# Revit family: Legrand XL³-S 160 saillie
name_source: partatom
category: Equipement électrique
units: mm (PartAtom-declared; Revit-internal decimal feet)

## family parameters
Basée sur le plan de construction = Non
Configuration du panneau = Deux colonnes, circuits au sein
Cote de connecteur circulaire = Utiliser le diamètre
Couper avec des vides une fois chargée = Non
Numéro OmniClass = 23.80.30.11.17
Partagée = Non
Point de calcul de pièce = Non
Titre OmniClass = Distribution Boards and Control Panels
Toujours verticalement = Oui
Type d'élément = Tableau de raccordement

## types (12) — shared parameters
Conditions Générale d'Utilisation = https://export.legrand.com
ETIM Class 6.0 = EC000261
Fabricant = Legrand
IK = 07
IP = 40
Image du type = XL3S160_saillie_337204_p_230125.jpg
Matière = Acier
RAL = 9003
URL = www.legrand.fr
distance coté zone d'installation = 135 mm  [stored 0.442913 ft]
porte = Oui
profondeur = 135 mm  [stored 0.442913 ft]
zero-valued in all types: Elévation par défaut

## per-type parameters (varying)
- Enveloppe de distribution - XL³ S 160 - Coffret saillie - Métal - 24 modules - 2 rangées: Coffret 337202=Oui; Coffret 337203=Non; Coffret 337204=Non; Coffret 337205=Non; Coffret 337206=Non; Coffret 337207=Non; Coffret 337208=Non; Coffret 337214=Non; Coffret 337215=Non; Coffret 337216=Non; Coffret 337217=Non; Coffret 337218=Non; Description=337202  Enveloppe de distribution - XL³ S 160 - Coffret saillie - Métal - 24 modules - 2 rangées; Hauteur=440 mm  [stored 1.44357 ft]; Largeur=595 mm  [stored 1.9521 ft]; Largeur zone d'installation=865 mm  [stored 2.83793 ft]; distance avant zone d'installation=595 mm  [stored 1.9521 ft]; porte 337252=Oui; porte 337253=Non; porte 337254=Non; porte 337255=Non; porte 337256=Non; porte 337257=Non; porte 337258=Non; porte 337264=Non; porte 337265=Non; porte 337266=Non; porte 337267=Non; porte 337268=Non; profondeur zone d'installation=730 mm  [stored 2.39501 ft]
- Enveloppe de distribution - XL³ S 160 - Coffret saillie - Métal - 24 modules - 3 rangées: Coffret 337202=Non; Coffret 337203=Oui; Coffret 337204=Non; Coffret 337205=Non; Coffret 337206=Non; Coffret 337207=Non; Coffret 337208=Non; Coffret 337214=Non; Coffret 337215=Non; Coffret 337216=Non; Coffret 337217=Non; Coffret 337218=Non; Description=337203  Enveloppe de distribution - XL³ S 160 - Coffret saillie - Métal - 24 modules - 3 rangées; Hauteur=590 mm  [stored 1.9357 ft]; Largeur=595 mm  [stored 1.9521 ft]; Largeur zone d'installation=865 mm  [stored 2.83793 ft]; distance avant zone d'installation=595 mm  [stored 1.9521 ft]; porte 337252=Non; porte 337253=Oui; porte 337254=Non; porte 337255=Non; porte 337256=Non; porte 337257=Non; porte 337258=Non; porte 337264=Non; porte 337265=Non; porte 337266=Non; porte 337267=Non; porte 337268=Non; profondeur zone d'installation=730 mm  [stored 2.39501 ft]
- Enveloppe de distribution - XL³ S 160 - Coffret saillie - Métal - 24 modules - 4 rangées: Coffret 337202=Non; Coffret 337203=Non; Coffret 337204=Oui; Coffret 337205=Non; Coffret 337206=Non; Coffret 337207=Non; Coffret 337208=Non; Coffret 337214=Non; Coffret 337215=Non; Coffret 337216=Non; Coffret 337217=Non; Coffret 337218=Non; Description=337204  Enveloppe de distribution - XL³ S 160 - Coffret saillie - Métal - 24 modules - 4 rangées; Hauteur=740 mm  [stored 2.42782 ft]; Largeur=595 mm  [stored 1.9521 ft]; Largeur zone d'installation=865 mm  [stored 2.83793 ft]; distance avant zone d'installation=595 mm  [stored 1.9521 ft]; porte 337252=Non; porte 337253=Non; porte 337254=Oui; porte 337255=Non; porte 337256=Non; porte 337257=Non; porte 337258=Non; porte 337264=Non; porte 337265=Non; porte 337266=Non; porte 337267=Non; porte 337268=Non; profondeur zone d'installation=730 mm  [stored 2.39501 ft]
- Enveloppe de distribution - XL³ S 160 - Coffret saillie - Métal - 24 modules - 5 rangées: Coffret 337202=Non; Coffret 337203=Non; Coffret 337204=Non; Coffret 337205=Oui; Coffret 337206=Non; Coffret 337207=Non; Coffret 337208=Non; Coffret 337214=Non; Coffret 337215=Non; Coffret 337216=Non; Coffret 337217=Non; Coffret 337218=Non; Description=337205  Enveloppe de distribution - XL³ S 160 - Coffret saillie - Métal - 24 modules - 6 rangées; Hauteur=890 mm  [stored 2.91995 ft]; Largeur=595 mm  [stored 1.9521 ft]; Largeur zone d'installation=865 mm  [stored 2.83793 ft]; distance avant zone d'installation=595 mm  [stored 1.9521 ft]; porte 337252=Non; porte 337253=Non; porte 337254=Non; porte 337255=Oui; porte 337256=Non; porte 337257=Non; porte 337258=Non; porte 337264=Non; porte 337265=Non; porte 337266=Non; porte 337267=Non; porte 337268=Non; profondeur zone d'installation=730 mm  [stored 2.39501 ft]
- Enveloppe de distribution - XL³ S 160 - Coffret saillie - Métal - 24 modules - 6 rangées: Coffret 337202=Non; Coffret 337203=Non; Coffret 337204=Non; Coffret 337205=Non; Coffret 337206=Oui; Coffret 337207=Non; Coffret 337208=Non; Coffret 337214=Non; Coffret 337215=Non; Coffret 337216=Non; Coffret 337217=Non; Coffret 337218=Non; Description=337206  Enveloppe de distribution - XL³ S 160 - Coffret saillie - Métal - 24 modules - 7 rangées; Hauteur=1040 mm  [stored 3.41207 ft]; Largeur=595 mm  [stored 1.9521 ft]; Largeur zone d'installation=865 mm  [stored 2.83793 ft]; distance avant zone d'installation=595 mm  [stored 1.9521 ft]; porte 337252=Non; porte 337253=Non; porte 337254=Non; porte 337255=Non; porte 337256=Oui; porte 337257=Non; porte 337258=Non; porte 337264=Non; porte 337265=Non; porte 337266=Non; porte 337267=Non; porte 337268=Non; profondeur zone d'installation=730 mm  [stored 2.39501 ft]
- Enveloppe de distribution - XL³ S 160 - Coffret saillie - Métal - 24 modules - 7 rangées: Coffret 337202=Non; Coffret 337203=Non; Coffret 337204=Non; Coffret 337205=Non; Coffret 337206=Non; Coffret 337207=Oui; Coffret 337208=Non; Coffret 337214=Non; Coffret 337215=Non; Coffret 337216=Non; Coffret 337217=Non; Coffret 337218=Non; Description=337207  Enveloppe de distribution - XL³ S 160 - Coffret saillie - Métal - 24 modules - 7 rangées; Hauteur=1190 mm  [stored 3.9042 ft]; Largeur=595 mm  [stored 1.9521 ft]; Largeur zone d'installation=865 mm  [stored 2.83793 ft]; distance avant zone d'installation=595 mm  [stored 1.9521 ft]; porte 337252=Non; porte 337253=Non; porte 337254=Non; porte 337255=Non; porte 337256=Non; porte 337257=Oui; porte 337258=Non; porte 337264=Non; porte 337265=Non; porte 337266=Non; porte 337267=Non; porte 337268=Non; profondeur zone d'installation=730 mm  [stored 2.39501 ft]
- Enveloppe de distribution - XL³ S 160 - Coffret saillie - Métal - 24 modules - 8 rangées: Coffret 337202=Non; Coffret 337203=Non; Coffret 337204=Non; Coffret 337205=Non; Coffret 337206=Non; Coffret 337207=Non; Coffret 337208=Oui; Coffret 337214=Non; Coffret 337215=Non; Coffret 337216=Non; Coffret 337217=Non; Coffret 337218=Non; Description=337208  Enveloppe de distribution - XL³ S 160 - Coffret saillie - Métal - 24 modules - 8 rangées; Hauteur=1340 mm  [stored 4.39633 ft]; Largeur=595 mm  [stored 1.9521 ft]; Largeur zone d'installation=865 mm  [stored 2.83793 ft]; distance avant zone d'installation=595 mm  [stored 1.9521 ft]; porte 337252=Non; porte 337253=Non; porte 337254=Non; porte 337255=Non; porte 337256=Non; porte 337257=Non; porte 337258=Oui; porte 337264=Non; porte 337265=Non; porte 337266=Non; porte 337267=Non; porte 337268=Non; profondeur zone d'installation=730 mm  [stored 2.39501 ft]
- Enveloppe de distribution - XL³ S 160 - Coffret saillie - Métal - 36 modules - 4 rangées: Coffret 337202=Non; Coffret 337203=Non; Coffret 337204=Non; Coffret 337205=Non; Coffret 337206=Non; Coffret 337207=Non; Coffret 337208=Non; Coffret 337214=Oui; Coffret 337215=Non; Coffret 337216=Non; Coffret 337217=Non; Coffret 337218=Non; Description=337214  Enveloppe de distribution - XL³ S 160 - Coffret saillie - Métal - 36 modules - 4 rangées; Hauteur=740 mm  [stored 2.42782 ft]; Largeur=810 mm; Largeur zone d'installation=1080 mm  [stored 3.54331 ft]; distance avant zone d'installation=810 mm; porte 337252=Non; porte 337253=Non; porte 337254=Non; porte 337255=Non; porte 337256=Non; porte 337257=Non; porte 337258=Non; porte 337264=Oui; porte 337265=Non; porte 337266=Non; porte 337267=Non; porte 337268=Non; profondeur zone d'installation=945 mm
- Enveloppe de distribution - XL³ S 160 - Coffret saillie - Métal - 36 modules - 5 rangées: Coffret 337202=Non; Coffret 337203=Non; Coffret 337204=Non; Coffret 337205=Non; Coffret 337206=Non; Coffret 337207=Non; Coffret 337208=Non; Coffret 337214=Non; Coffret 337215=Oui; Coffret 337216=Non; Coffret 337217=Non; Coffret 337218=Non; Description=337215  Enveloppe de distribution - XL³ S 160 - Coffret saillie - Métal - 36 modules - 5 rangées; Hauteur=890 mm  [stored 2.91995 ft]; Largeur=810 mm; Largeur zone d'installation=1080 mm  [stored 3.54331 ft]; distance avant zone d'installation=810 mm; porte 337252=Non; porte 337253=Non; porte 337254=Non; porte 337255=Non; porte 337256=Non; porte 337257=Non; porte 337258=Non; porte 337264=Non; porte 337265=Oui; porte 337266=Non; porte 337267=Non; porte 337268=Non; profondeur zone d'installation=945 mm
- Enveloppe de distribution - XL³ S 160 - Coffret saillie - Métal - 36 modules - 6 rangées: Coffret 337202=Non; Coffret 337203=Non; Coffret 337204=Non; Coffret 337205=Non; Coffret 337206=Non; Coffret 337207=Non; Coffret 337208=Non; Coffret 337214=Non; Coffret 337215=Non; Coffret 337216=Oui; Coffret 337217=Non; Coffret 337218=Non; Description=337216  Enveloppe de distribution - XL³ S 160 - Coffret saillie - Métal - 36 modules - 6 rangées; Hauteur=1040 mm  [stored 3.41207 ft]; Largeur=810 mm; Largeur zone d'installation=1080 mm  [stored 3.54331 ft]; distance avant zone d'installation=810 mm; porte 337252=Non; porte 337253=Non; porte 337254=Non; porte 337255=Non; porte 337256=Non; porte 337257=Non; porte 337258=Non; porte 337264=Non; porte 337265=Non; porte 337266=Oui; porte 337267=Non; porte 337268=Non; profondeur zone d'installation=945 mm
- Enveloppe de distribution - XL³ S 160 - Coffret saillie - Métal - 36 modules - 7 rangées: Coffret 337202=Non; Coffret 337203=Non; Coffret 337204=Non; Coffret 337205=Non; Coffret 337206=Non; Coffret 337207=Non; Coffret 337208=Non; Coffret 337214=Non; Coffret 337215=Non; Coffret 337216=Non; Coffret 337217=Oui; Coffret 337218=Non; Description=337217  Enveloppe de distribution - XL³ S 160 - Coffret saillie - Métal - 36 modules - 7 rangées; Hauteur=1190 mm  [stored 3.9042 ft]; Largeur=810 mm; Largeur zone d'installation=1080 mm  [stored 3.54331 ft]; distance avant zone d'installation=810 mm; porte 337252=Non; porte 337253=Non; porte 337254=Non; porte 337255=Non; porte 337256=Non; porte 337257=Non; porte 337258=Non; porte 337264=Non; porte 337265=Non; porte 337266=Non; porte 337267=Oui; porte 337268=Non; profondeur zone d'installation=945 mm
- Enveloppe de distribution - XL³ S 160 - Coffret saillie - Métal - 36 modules - 8 rangées: Coffret 337202=Non; Coffret 337203=Non; Coffret 337204=Non; Coffret 337205=Non; Coffret 337206=Non; Coffret 337207=Non; Coffret 337208=Non; Coffret 337214=Non; Coffret 337215=Non; Coffret 337216=Non; Coffret 337217=Non; Coffret 337218=Oui; Description=337218  Enveloppe de distribution - XL³ S 160 - Coffret saillie - Métal - 36 modules - 8 rangées; Hauteur=1340 mm  [stored 4.39633 ft]; Largeur=810 mm; Largeur zone d'installation=1080 mm  [stored 3.54331 ft]; distance avant zone d'installation=810 mm; porte 337252=Non; porte 337253=Non; porte 337254=Non; porte 337255=Non; porte 337256=Non; porte 337257=Non; porte 337258=Non; porte 337264=Non; porte 337265=Non; porte 337266=Non; porte 337267=Non; porte 337268=Oui; profondeur zone d'installation=945 mm

note: [stored X ft] marks values corroborated as IEEE doubles in the binary element streams (Revit-internal decimal feet)
